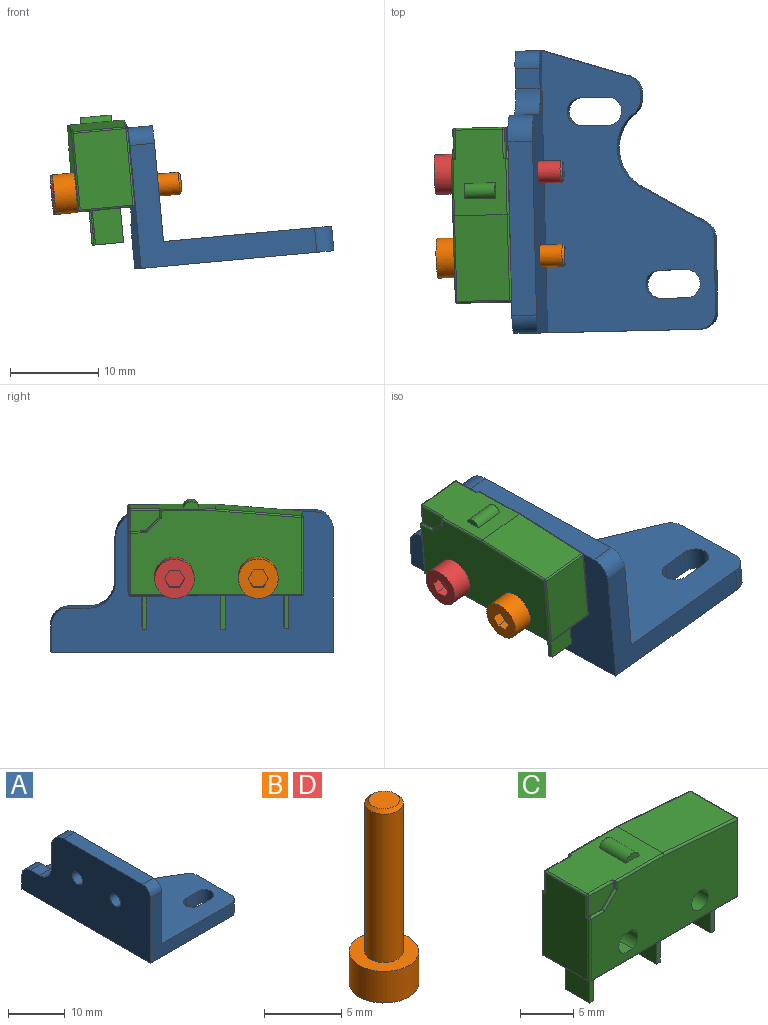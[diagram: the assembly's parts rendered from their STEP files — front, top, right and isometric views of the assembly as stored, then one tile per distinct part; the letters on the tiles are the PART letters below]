
ASSEMBLY  parts=4 mates=3
PART A: 32 faces, bbox 22x32x16 mm
  f0: plane 32x19.2mm, normal (0,0,1), area 394.5mm2, adj f3,f4,f5,f6,f7,f8,f9,f10
  f1: plane 3.1x2.8mm, normal (0,1,0), area 8.7mm2, adj f2,f20,f21,f30,f31
  f2: plane 32x16mm, normal (-1,0,0), area 421mm2, adj f1,f3,f21,f22,f23,f24,f25,f26
  f3: plane 20x14mm, normal (0,-1,0), area 87.4mm2, adj f0,f2,f4,f21,f22,f31
  f4: cylinder r=2mm len=2.8mm, axis (0,0,-1), area 8.8mm2, adj f0,f3,f5,f21
  f5: plane 8.39x2.8mm, normal (1,0,0), area 23.5mm2, adj f0,f4,f6,f21
  f6: cylinder r=2mm len=2.8mm, axis (0,0,-1), area 5.9mm2, adj f0,f5,f7,f21
  f7: plane 7.3x4.21mm, normal (0.5,0.87,0), area 23.6mm2, adj f0,f6,f8,f21
  f8: cylinder r=5mm len=8.33mm, axis (0,0,-1), area 27.6mm2, adj f0,f7,f9,f21
  f9: cylinder r=2mm len=2.8mm, axis (0,0,-1), area 5.2mm2, adj f0,f8,f10,f21
  f10: plane 2.8x0.73mm, normal (1,0,0), area 2mm2, adj f0,f9,f11,f21
  f11: cylinder r=2mm len=2.8mm, axis (0,0,-1), area 7.1mm2, adj f0,f10,f20,f21
  f12: cylinder r=1.6mm len=3.2mm, axis (0,0,-1), area 14.1mm2, adj f0,f13,f18,f21
  f13: plane 3x2.8mm, normal (0,-1,0), area 8.4mm2, adj f0,f12,f14,f21
  f14: cylinder r=1.6mm len=3.2mm, axis (0,0,-1), area 14.1mm2, adj f0,f13,f18,f21
  f15: cylinder r=1.6mm len=3.2mm, axis (0,0,-1), area 14.1mm2, adj f0,f16,f19,f21
  f16: plane 3x2.8mm, normal (0,1,0), area 8.4mm2, adj f0,f15,f17,f21
  f17: cylinder r=1.6mm len=3.2mm, axis (0,0,-1), area 14.1mm2, adj f0,f16,f19,f21
  f18: plane 3x2.8mm, normal (0,1,0), area 8.4mm2, adj f0,f12,f14,f21
  f19: plane 3x2.8mm, normal (0,-1,0), area 8.4mm2, adj f0,f15,f17,f21
  f20: plane 9.8x3.09mm, normal (0.3,0.95,0), area 28.8mm2, adj f0,f1,f11,f21
  f21: plane 32x22mm, normal (0,0,-1), area 484.1mm2, adj f1,f2,f3,f4,f5,f6,f7,f8
  f22: cylinder r=2mm len=2.8mm, axis (-1,0,0), area 8.8mm2, adj f2,f3,f23,f31
  f23: plane 19.71x2.8mm, normal (0,0,1), area 55.2mm2, adj f2,f22,f24,f31
  f24: cylinder r=3mm len=3mm, axis (-1,0,0), area 13.2mm2, adj f2,f23,f25,f31
  f25: plane 4.9x2.8mm, normal (0,1,0), area 13.7mm2, adj f2,f24,f26,f31
  f26: cylinder r=3mm len=3mm, axis (-1,0,0), area 13.2mm2, adj f2,f25,f27,f31
  f27: plane 2.8x2.29mm, normal (0,0,1), area 6.4mm2, adj f2,f26,f30,f31
  f28: cylinder r=1.25mm len=2.8mm, axis (-1,0,0), area 22mm2, adj f2,f31
  f29: cylinder r=1.25mm len=2.8mm, axis (-1,0,0), area 22mm2, adj f2,f31
  f30: cylinder r=2mm len=2.8mm, axis (-1,0,0), area 8.8mm2, adj f1,f2,f27,f31
  f31: plane 32x13.2mm, normal (1,0,0), area 331.4mm2, adj f0,f1,f3,f22,f23,f24,f25,f26
PART B: 13 faces, bbox 4.5x4.5x14.5 mm
  f0: plane 4.5x4.5mm, normal (0,0,-1), area 12.4mm2, adj f2,f6,f7,f8,f9,f10,f11
  f1: plane 2x2mm, normal (0,0,1), area 3.1mm2, adj f5
  f2: cylinder r=2.25mm len=4.5mm, axis (0,0,-1), area 35.3mm2, adj f0,f3
  f3: plane 4.5x4.5mm, normal (0,0,1), area 11mm2, adj f2,f4
  f4: cylinder r=1.25mm len=11.75mm, axis (0,0,-1), area 92.3mm2, adj f3,f5
  f5: cone r=1.25mm half-angle=45deg, axis (0,0,-1), area 2.5mm2, adj f1,f4
  f6: plane 1.15x1.1mm, normal (-1,0,0), area 1.3mm2, adj f0,f7,f11,f12
  f7: plane 1.1x1mm, normal (-0.5,-0.87,0), area 1.3mm2, adj f0,f6,f8,f12
  f8: plane 1.1x1mm, normal (0.5,-0.87,0), area 1.3mm2, adj f0,f7,f9,f12
  f9: plane 1.15x1.1mm, normal (1,0,0), area 1.3mm2, adj f0,f8,f10,f12
  f10: plane 1.1x1mm, normal (0.5,0.87,0), area 1.3mm2, adj f0,f9,f11,f12
  f11: plane 1.1x1mm, normal (-0.5,0.87,0), area 1.3mm2, adj f0,f6,f10,f12
  f12: plane 2.31x2mm, normal (0,0,-1), area 3.5mm2, adj f6,f7,f8,f9,f10,f11
PART C: 80 faces, bbox 19.9x6.5x14.6 mm
  f0: plane 1.7x0.1mm, normal (0,0,1), area 0.2mm2, adj f1,f15,f19,f26
  f1: plane 1.6x1.6mm, normal (-0.71,0,0.71), area 0.2mm2, adj f0,f15,f21,f48
  f2: sphere r=0.2mm, area 0.1mm2, adj f19,f26,f27
  f3: sphere r=0.2mm, area 0mm2, adj f27,f32,f33
  f4: plane 3.2x0.5mm, normal (0,0,-1), area 1.6mm2, adj f5,f6,f34,f35
  f5: plane 3.9x0.5mm, normal (0,-1,0), area 2mm2, adj f4,f34,f35,f60
  f6: plane 3.9x0.5mm, normal (0,1,0), area 2mm2, adj f4,f34,f35,f60
  f7: plane 3.2x0.5mm, normal (0,0,-1), area 1.6mm2, adj f8,f9,f36,f37
  f8: plane 3.9x0.5mm, normal (0,-1,0), area 2mm2, adj f7,f36,f37,f60
  f9: plane 3.9x0.5mm, normal (0,1,0), area 2mm2, adj f7,f36,f37,f60
  f10: plane 3.2x0.5mm, normal (0,0,-1), area 1.6mm2, adj f11,f12,f38,f39
  f11: plane 3.9x0.5mm, normal (0,-1,0), area 2mm2, adj f10,f38,f39,f60
  f12: plane 3.9x0.5mm, normal (0,1,0), area 2mm2, adj f10,f38,f39,f60
  f13: sphere r=0.2mm, area 0.1mm2, adj f33,f40,f41
  f14: sphere r=0.2mm, area 0.1mm2, adj f40,f42,f43
  f15: plane 3.3x2.3mm, normal (0,1,0), area 6.3mm2, adj f0,f1,f31,f48,f49
  f16: sphere r=0.2mm, area 0.1mm2, adj f31,f49,f50
  f17: sphere r=0.2mm, area 0.1mm2, adj f30,f50,f51
  f18: cylinder r=1.25mm len=6.4mm, axis (0,-1,0), area 17.2mm2, adj f52,f53,f54,f79
  f19: cylinder r=0.2mm len=1.7mm, axis (1,0,0), area 0.5mm2, adj f0,f2,f20,f54
  f20: bspline ~0.2x0.2mm, area 0mm2, adj f19,f21,f54
  f21: cylinder r=0.2mm len=1.74mm, axis (0.71,0,0.71), area 0.7mm2, adj f1,f20,f22,f54
  f22: bspline ~0.2x0.2mm, area 0mm2, adj f21,f23,f54
  f23: cylinder r=0.2mm len=0.9mm, axis (0,0,1), area 0.3mm2, adj f22,f47,f48,f54
  f24: plane 3.3x2.3mm, normal (0,-1,0), area 6.3mm2, adj f30,f51,f55,f56,f66
  f25: bspline ~0.2x0.2mm, area 0mm2, adj f26,f31,f58
  f26: cylinder r=0.2mm len=0.2mm, axis (0,1,0), area 0mm2, adj f0,f2,f25,f58
  f27: cylinder r=0.2mm len=7mm, axis (0,0,1), area 2.2mm2, adj f2,f3,f54,f58
  f28: cylinder r=0.2mm len=0.2mm, axis (0,1,0), area 0mm2, adj f29,f56,f57,f58
  f29: bspline ~0.2x0.2mm, area 0mm2, adj f28,f30,f58
  f30: cylinder r=0.2mm len=2.3mm, axis (0,0,1), area 0.7mm2, adj f17,f24,f29,f58
  f31: cylinder r=0.2mm len=2.3mm, axis (0,0,-1), area 0.7mm2, adj f15,f16,f25,f58
  f32: cylinder r=0.2mm len=6mm, axis (0,-1,0), area 1.9mm2, adj f3,f58,f59,f60
  f33: cylinder r=0.2mm len=19.4mm, axis (1,0,0), area 6.1mm2, adj f3,f13,f54,f60
  f34: plane 3.9x3.2mm, normal (1,0,0), area 12.5mm2, adj f4,f5,f6,f60
  f35: plane 3.9x3.2mm, normal (-1,0,0), area 12.5mm2, adj f4,f5,f6,f60
  f36: plane 3.9x3.2mm, normal (1,0,0), area 12.5mm2, adj f7,f8,f9,f60
  f37: plane 3.9x3.2mm, normal (-1,0,0), area 12.5mm2, adj f7,f8,f9,f60
  f38: plane 3.9x3.2mm, normal (1,0,0), area 12.5mm2, adj f10,f11,f12,f60
  f39: plane 3.9x3.2mm, normal (-1,0,0), area 12.5mm2, adj f10,f11,f12,f60
  f40: cylinder r=0.2mm len=8.72mm, axis (0,0,1), area 2.7mm2, adj f13,f14,f54,f61
  f41: cylinder r=0.2mm len=6mm, axis (0,-1,0), area 1.9mm2, adj f13,f60,f61,f62
  f42: cylinder r=0.2mm len=9.73mm, axis (-1,0,0.08), area 3.1mm2, adj f14,f47,f54,f63
  f43: cylinder r=0.2mm len=6mm, axis (0,-1,0), area 1.8mm2, adj f14,f61,f63,f64
  f44: plane 1.76x0.7mm, normal (0,1,0), area 0.9mm2, adj f46,f65
  f45: plane 1.76x0.7mm, normal (0,-1,0), area 0.9mm2, adj f46,f65
  f46: cylinder r=0.9mm len=3.5mm, axis (0,-1,0), area 8.5mm2, adj f44,f45,f65
  f47: cylinder r=0.2mm len=6.4mm, axis (1,0,0), area 2mm2, adj f23,f42,f54,f65
  f48: plane 0.9x0.3mm, normal (-1,0,0), area 0.1mm2, adj f1,f15,f23,f49,f65
  f49: cylinder r=0.2mm len=3.3mm, axis (-1,0,0), area 1mm2, adj f15,f16,f48,f65
  f50: cylinder r=0.2mm len=5.4mm, axis (0,-1,0), area 1.7mm2, adj f16,f17,f58,f65
  f51: cylinder r=0.2mm len=3.3mm, axis (1,0,0), area 1mm2, adj f17,f24,f65,f66
  f52: plane 6.4x1.19mm, normal (0,0,1), area 7.6mm2, adj f18,f54,f67,f79
  f53: plane 6.4x1.19mm, normal (0,0,-1), area 7.6mm2, adj f18,f54,f67,f79
  f54: plane 19.4x9.5mm, normal (0,1,0), area 164.7mm2, adj f18,f19,f20,f21,f22,f23,f27,f33
  f55: plane 1.6x1.6mm, normal (-0.71,0,0.71), area 0.2mm2, adj f24,f56,f66,f69
  f56: plane 1.7x0.1mm, normal (0,0,1), area 0.2mm2, adj f24,f28,f55,f71
  f57: sphere r=0.2mm, area 0.1mm2, adj f28,f71,f72
  f58: plane 9.56x6.06mm, normal (-1,0,0), area 55.5mm2, adj f25,f26,f27,f28,f29,f30,f31,f32
  f59: sphere r=0.2mm, area 0.1mm2, adj f32,f72,f73
  f60: plane 19.4x6mm, normal (0,0,-1), area 111.6mm2, adj f5,f6,f8,f9,f11,f12,f32,f33
  f61: plane 8.72x6mm, normal (1,0,0), area 52.3mm2, adj f40,f41,f43,f74
  f62: sphere r=0.2mm, area 0.1mm2, adj f41,f73,f74
  f63: plane 9.72x6mm, normal (0.08,0,1), area 58.5mm2, adj f42,f43,f65,f75
  f64: sphere r=0.2mm, area 0.1mm2, adj f43,f74,f75
  f65: plane 9.7x6mm, normal (0,0,1), area 50.1mm2, adj f44,f45,f46,f47,f48,f49,f50,f51
  f66: plane 0.9x0.3mm, normal (-1,0,0), area 0.1mm2, adj f24,f51,f55,f65,f77
  f67: cylinder r=1.25mm len=6.4mm, axis (0,-1,0), area 17.2mm2, adj f52,f53,f54,f79
  f68: cylinder r=1.1mm len=6.4mm, axis (0,-1,0), area 44.2mm2, adj f54,f79
  f69: cylinder r=0.2mm len=1.74mm, axis (-0.71,0,-0.71), area 0.7mm2, adj f55,f70,f78,f79
  f70: bspline ~0.2x0.2mm, area 0mm2, adj f69,f71,f79
  f71: cylinder r=0.2mm len=1.7mm, axis (-1,0,0), area 0.5mm2, adj f56,f57,f70,f79
  f72: cylinder r=0.2mm len=7mm, axis (0,0,1), area 2.2mm2, adj f57,f58,f59,f79
  f73: cylinder r=0.2mm len=19.4mm, axis (-1,0,0), area 6.1mm2, adj f59,f60,f62,f79
  f74: cylinder r=0.2mm len=8.72mm, axis (0,0,-1), area 2.7mm2, adj f61,f62,f64,f79
  f75: cylinder r=0.2mm len=9.73mm, axis (1,0,-0.08), area 3.1mm2, adj f63,f64,f76,f79
  f76: cylinder r=0.2mm len=6.4mm, axis (1,0,0), area 2mm2, adj f65,f75,f77,f79
  f77: cylinder r=0.2mm len=0.9mm, axis (0,0,-1), area 0.3mm2, adj f66,f76,f78,f79
  f78: bspline ~0.2x0.2mm, area 0mm2, adj f69,f77,f79
  f79: plane 19.41x9.51mm, normal (0,-1,0), area 164.7mm2, adj f18,f52,f53,f67,f68,f69,f70,f71
PART D: same geometry as B
PLACE A rot(axis=(-0.01,-0.97,0.24),5.4deg) t=(-41.79,-41.32,9.5)mm fixed
PLACE B rot(axis=(-0.01,1,0.01),84.8deg) t=(-3.75,-81.65,62.43)mm
PLACE C rot(axis=(0.05,-0.05,-1),88.8deg) t=(4.54,-26.78,20.82)mm
PLACE D rot(axis=(-0.01,1,0.01),84.8deg) t=(-3.96,-72.16,62.41)mm
MATE fastened C.f18 <-> A.f29  axis (1,0.02,0.09) through (7.42,-21.96,23.3)mm
MATE fastened B.f2 <-> C.f68  axis (-1,-0.02,-0.09) through (1.27,-31.6,22.73)mm
MATE fastened D.f2 <-> C.f18  axis (1,0.02,0.09) through (1.05,-22.1,22.71)mm
